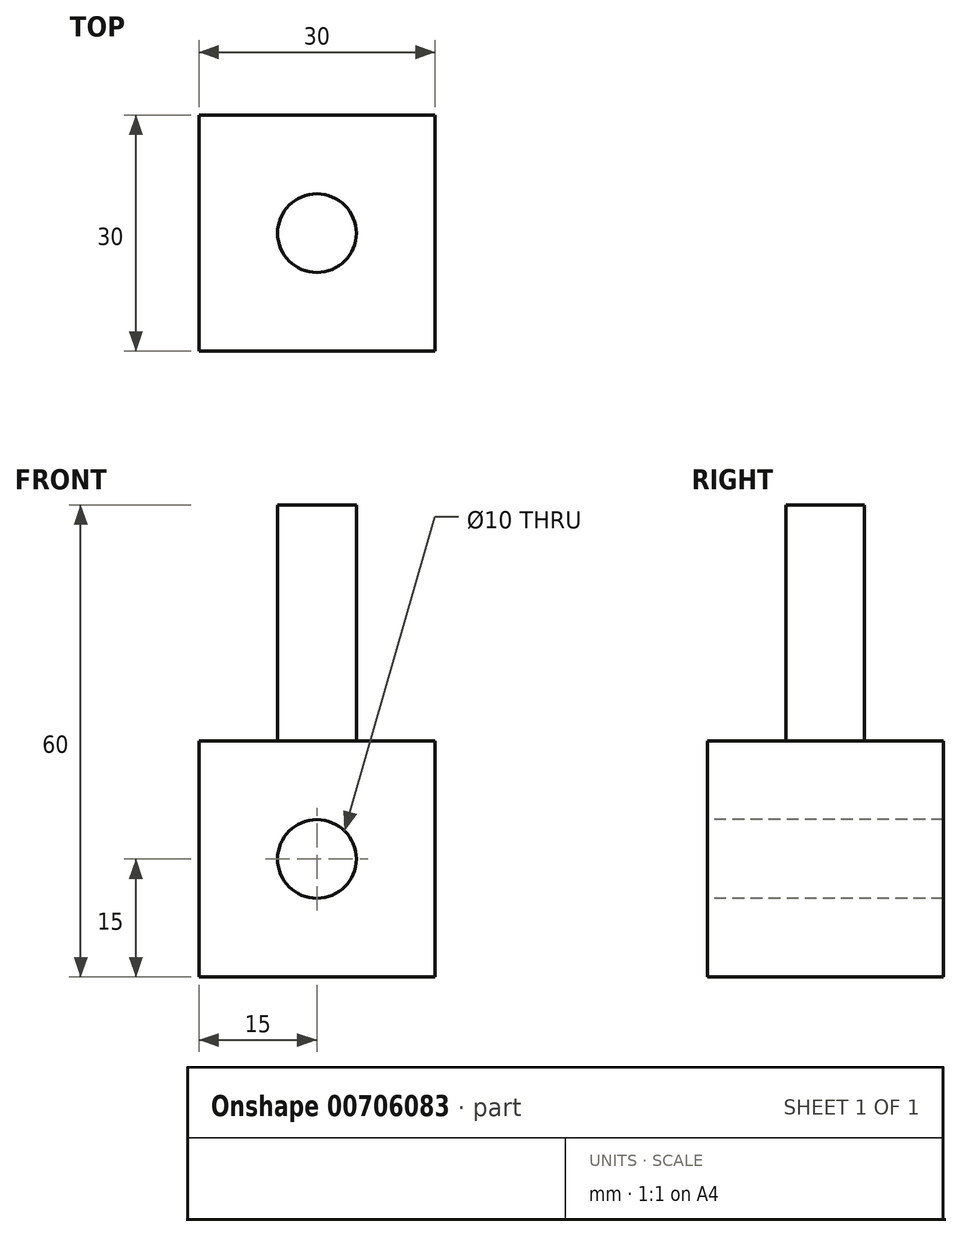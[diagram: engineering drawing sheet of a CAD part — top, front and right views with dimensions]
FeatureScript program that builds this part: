
annotation { "Feature Type Name" : "Feature", "Feature Type Description" : "" }
export const myFeature = defineFeature(function(context is Context, id is Id, definition is map)
    precondition{}
    {
        {
            var Q0;
            Q0=qCreatedBy(makeId("Front.planeOp"),FACE);
            var sketch = newSketch(context, id + "F0", { "sketchPlane" : qUnion([Q0])});
            skLineSegment(sketch, "E0.bottom", {"start": v(15, 15) * mm, "end": v(-15, 15) * mm});
            skLineSegment(sketch, "E0.top", {"start": v(15, -15) * mm, "end": v(-15, -15) * mm});
            skLineSegment(sketch, "E0.left", {"start": v(15, 15) * mm, "end": v(15, -15) * mm});
            skLineSegment(sketch, "E0.right", {"start": v(-15, 15) * mm, "end": v(-15, -15) * mm});
            skPoint(sketch, "E0.middle", {"position": v(0, 0) * mm});
            skSolve(sketch);
        }
        {
            var Q0;
            Q0=makeQuery(id+"F0.imprint","IMPRINT",FACE,{"disambiguationData":[TD([[makeQuery(id+"F0.imprint","IMPRINT",EDGE,{"derivedFrom":sQuery(id+"F0.wireOp",EDGE,"E0.bottom")}),1.0]])]});
            extrude(context, id + "F1", {"entities" : qUnion([Q0]), "depth" : 30 * mm, "offsetDistance" : 25 * mm});
        }
        {
            var Q0;
            Q0=makeQuery(id+"F1.opExtrude","CAP_FACE",FACE,{"disambiguationData":[OSD([sQuery(id+"F0.wireOp",EDGE,"E0.bottom"),sQuery(id+"F0.wireOp",EDGE,"E0.top"),sQuery(id+"F0.wireOp",EDGE,"E0.left"),sQuery(id+"F0.wireOp",EDGE,"E0.right")])],"isStart":false});
            var sketch = newSketch(context, id + "F2", { "sketchPlane" : qUnion([Q0])});
            skCircle(sketch, "E1", {"center": v(0, 0) * mm, "radius": 5 * mm});
            skSolve(sketch);
        }
        {
            var Q0;
            Q0=makeQuery(id+"F2.imprint","IMPRINT",FACE,{"disambiguationData":[TD([[makeQuery(id+"F2.imprint","IMPRINT",EDGE,{"derivedFrom":sQuery(id+"F2.wireOp",EDGE,"E1")}),1.0]])]});
            extrude(context, id + "F3", {"entities" : qUnion([Q0]), "operationType" : NewBodyOperationType.REMOVE, "oppositeDirection" : true, "depth" : 30 * mm, "offsetDistance" : 25 * mm});
        }
        {
            var Q0;
            Q0=makeQuery(id+"F1.opExtrude","SWEPT_FACE",FACE,{"disambiguationData":[OSD([sQuery(id+"F0.wireOp",EDGE,"E0.bottom")])]});
            var sketch = newSketch(context, id + "F4", { "sketchPlane" : qUnion([Q0])});
            skCircle(sketch, "E2", {"center": v(0, -15) * mm, "radius": 5 * mm});
            skPoint(sketch, "E2.centerSnap0", {"position": v(-15, -15) * mm});
            skSolve(sketch);
        }
        {
            var Q0;
            Q0=makeQuery(id+"F4.imprint","IMPRINT",FACE,{"disambiguationData":[TD([[makeQuery(id+"F4.imprint","IMPRINT",EDGE,{"derivedFrom":sQuery(id+"F4.wireOp",EDGE,"E2")}),1.0]])]});
            extrude(context, id + "F5", {"entities" : qUnion([Q0]), "operationType" : NewBodyOperationType.ADD, "depth" : 30 * mm, "offsetDistance" : 25 * mm});
        }
    });
